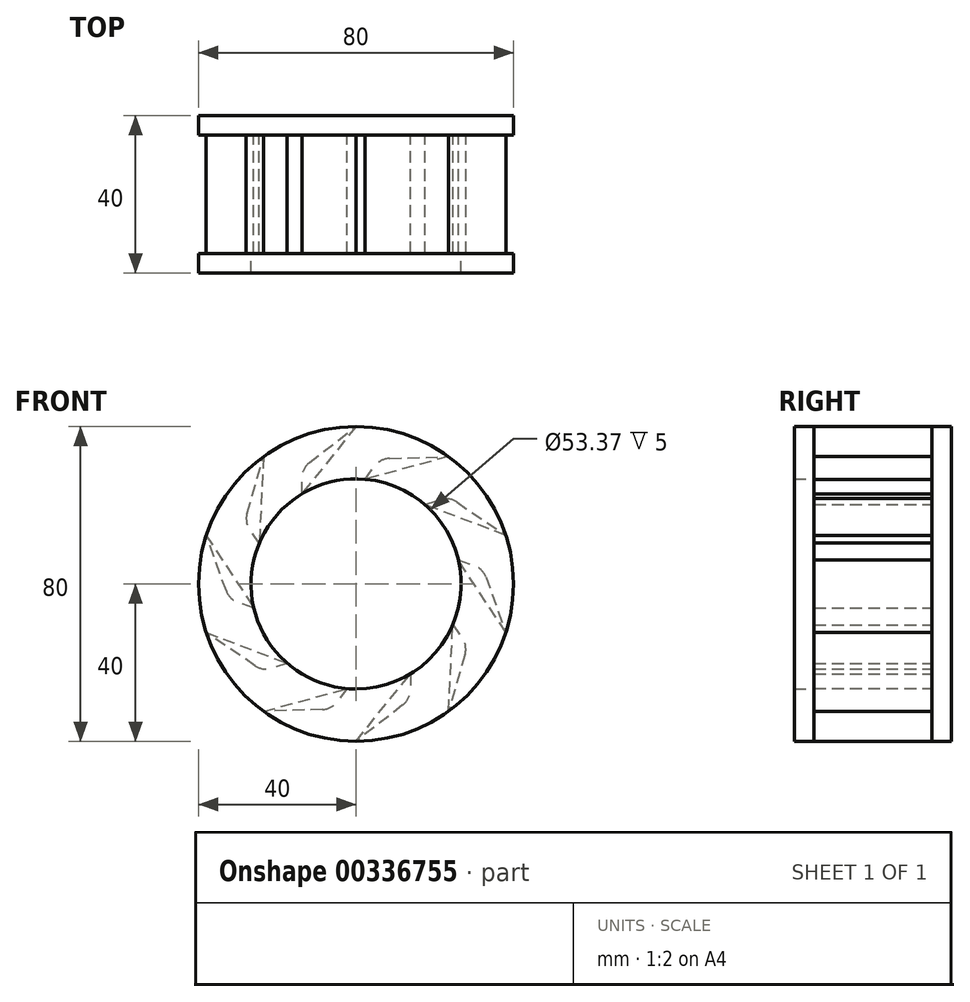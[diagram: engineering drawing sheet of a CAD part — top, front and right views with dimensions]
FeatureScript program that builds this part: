
annotation { "Feature Type Name" : "Feature", "Feature Type Description" : "" }
export const myFeature = defineFeature(function(context is Context, id is Id, definition is map)
    precondition{}
    {
        {
            var Q0;
            Q0=qCreatedBy(makeId("Front.planeOp"),FACE);
            var sketch = newSketch(context, id + "F0", { "sketchPlane" : qUnion([Q0])});
            skLineSegment(sketch, "E0", {"start": v(0, 55.71) * mm, "end": v(0, -58.93) * mm, "construction": true});
            skLineSegment(sketch, "E1", {"start": v(-76.6, 0) * mm, "end": v(92.9, 0) * mm, "construction": true});
            skCircle(sketch, "E2", {"center": v(0, 0) * mm, "radius": 40 * mm});
            skSolve(sketch);
        }
        {
            var Q0;
            Q0=makeQuery(id+"F0.imprint","IMPRINT",FACE,{"disambiguationData":[TD([[makeQuery(id+"F0.imprint","IMPRINT",EDGE,{"derivedFrom":sQuery(id+"F0.wireOp",EDGE,"E2")}),1.0]])]});
            extrude(context, id + "F1", {"entities" : qUnion([Q0]), "depth" : 5 * mm});
        }
        {
            var Q0;
            Q0=makeQuery(id+"F1.opExtrude","CAP_FACE",FACE,{"disambiguationData":[OSD([sQuery(id+"F0.wireOp",EDGE,"E2")])],"isStart":false});
            var sketch = newSketch(context, id + "F2", { "sketchPlane" : qUnion([Q0])});
            skLineSegment(sketch, "E3", {"start": v(0, 40) * mm, "end": v(-13.78, 22.85) * mm});
            skLineSegment(sketch, "E4", {"start": v(-13.78, 22.85) * mm, "end": v(-13.78, 26.85) * mm});
            skLineSegment(sketch, "E5", {"start": v(-11.85, 30.8) * mm, "end": v(0, 40) * mm});
            skPoint(sketch, "E6.visualSharp", {"position": v(-13.78, 29.3) * mm});
            skArc(sketch, "E6.filletArc", {"start": v(-11.85, 30.8) * mm, "mid": v(-13.27, 29.05) * mm, "end": v(-13.78, 26.85) * mm});
            skLineSegment(sketch, "E7.1.0", {"start": v(-27.69, 17.95) * mm, "end": v(-23.51, 32.36) * mm});
            skArc(sketch, "E7.1.1", {"start": v(-27.69, 17.95) * mm, "mid": v(-27.81, 15.7) * mm, "end": v(-26.93, 13.62) * mm});
            skLineSegment(sketch, "E7.1.2", {"start": v(-24.58, 10.39) * mm, "end": v(-26.93, 13.62) * mm});
            skLineSegment(sketch, "E7.1.3", {"start": v(-23.51, 32.36) * mm, "end": v(-24.58, 10.39) * mm});
            skLineSegment(sketch, "E7.2.0", {"start": v(-32.95, -1.75) * mm, "end": v(-38.04, 12.36) * mm});
            skArc(sketch, "E7.2.1", {"start": v(-32.95, -1.75) * mm, "mid": v(-31.73, -3.65) * mm, "end": v(-29.8, -4.8) * mm});
            skLineSegment(sketch, "E7.2.2", {"start": v(-26, -6.04) * mm, "end": v(-29.8, -4.8) * mm});
            skLineSegment(sketch, "E7.2.3", {"start": v(-38.04, 12.36) * mm, "end": v(-26, -6.04) * mm});
            skLineSegment(sketch, "E7.3.0", {"start": v(-25.63, -20.79) * mm, "end": v(-38.04, -12.36) * mm});
            skArc(sketch, "E7.3.1", {"start": v(-25.63, -20.79) * mm, "mid": v(-23.53, -21.6) * mm, "end": v(-21.28, -21.4) * mm});
            skLineSegment(sketch, "E7.3.2", {"start": v(-17.47, -20.17) * mm, "end": v(-21.28, -21.4) * mm});
            skLineSegment(sketch, "E7.3.3", {"start": v(-38.04, -12.36) * mm, "end": v(-17.47, -20.17) * mm});
            skLineSegment(sketch, "E7.4.0", {"start": v(-8.52, -31.88) * mm, "end": v(-23.51, -32.36) * mm});
            skArc(sketch, "E7.4.1", {"start": v(-8.52, -31.88) * mm, "mid": v(-6.34, -31.3) * mm, "end": v(-4.63, -29.82) * mm});
            skLineSegment(sketch, "E7.4.2", {"start": v(-2.28, -26.59) * mm, "end": v(-4.63, -29.82) * mm});
            skLineSegment(sketch, "E7.4.3", {"start": v(-23.51, -32.36) * mm, "end": v(-2.28, -26.59) * mm});
            skLineSegment(sketch, "E7.5.0", {"start": v(11.85, -30.8) * mm, "end": v(0, -40) * mm});
            skArc(sketch, "E7.5.1", {"start": v(11.85, -30.8) * mm, "mid": v(13.27, -29.05) * mm, "end": v(13.78, -26.85) * mm});
            skLineSegment(sketch, "E7.5.2", {"start": v(13.78, -22.85) * mm, "end": v(13.78, -26.85) * mm});
            skLineSegment(sketch, "E7.5.3", {"start": v(0, -40) * mm, "end": v(13.78, -22.85) * mm});
            skLineSegment(sketch, "E7.6.0", {"start": v(27.69, -17.95) * mm, "end": v(23.51, -32.36) * mm});
            skArc(sketch, "E7.6.1", {"start": v(27.69, -17.95) * mm, "mid": v(27.81, -15.7) * mm, "end": v(26.93, -13.62) * mm});
            skLineSegment(sketch, "E7.6.2", {"start": v(24.58, -10.39) * mm, "end": v(26.93, -13.62) * mm});
            skLineSegment(sketch, "E7.6.3", {"start": v(23.51, -32.36) * mm, "end": v(24.58, -10.39) * mm});
            skLineSegment(sketch, "E7.7.0", {"start": v(32.95, 1.75) * mm, "end": v(38.04, -12.36) * mm});
            skArc(sketch, "E7.7.1", {"start": v(32.95, 1.75) * mm, "mid": v(31.73, 3.65) * mm, "end": v(29.8, 4.8) * mm});
            skLineSegment(sketch, "E7.7.2", {"start": v(26, 6.04) * mm, "end": v(29.8, 4.8) * mm});
            skLineSegment(sketch, "E7.7.3", {"start": v(38.04, -12.36) * mm, "end": v(26, 6.04) * mm});
            skLineSegment(sketch, "E7.8.0", {"start": v(25.63, 20.79) * mm, "end": v(38.04, 12.36) * mm});
            skArc(sketch, "E7.8.1", {"start": v(25.63, 20.79) * mm, "mid": v(23.53, 21.6) * mm, "end": v(21.28, 21.4) * mm});
            skLineSegment(sketch, "E7.8.2", {"start": v(17.47, 20.17) * mm, "end": v(21.28, 21.4) * mm});
            skLineSegment(sketch, "E7.8.3", {"start": v(38.04, 12.36) * mm, "end": v(17.47, 20.17) * mm});
            skLineSegment(sketch, "E7.9.0", {"start": v(8.52, 31.88) * mm, "end": v(23.51, 32.36) * mm});
            skArc(sketch, "E7.9.1", {"start": v(8.52, 31.88) * mm, "mid": v(6.34, 31.3) * mm, "end": v(4.63, 29.82) * mm});
            skLineSegment(sketch, "E7.9.2", {"start": v(2.28, 26.59) * mm, "end": v(4.63, 29.82) * mm});
            skLineSegment(sketch, "E7.9.3", {"start": v(23.51, 32.36) * mm, "end": v(2.28, 26.59) * mm});
            skPoint(sketch, "E7.center", {"position": v(0, 0) * mm});
            skSolve(sketch);
        }
        {
            var Q0;
            Q0 = qSketchRegion(id + "F2", true);
            extrude(context, id + "F3", {"entities" : qUnion([Q0]), "operationType" : NewBodyOperationType.ADD, "depth" : 30 * mm});
        }
        {
            var Q0;
            Q0=qCreatedBy(makeId("Front.planeOp"),FACE);
            cPlane(context, id + "F4", {"entities" : qUnion([Q0]), "cplaneType" : CPlaneType.OFFSET, "offset" : 35 * mm, "width" : 150 * mm, "height" : 150 * mm});
        }
        {
            var Q0;
            Q0=qCreatedBy(id+"F4.planeOp",FACE);
            var sketch = newSketch(context, id + "F5", { "sketchPlane" : qUnion([Q0])});
            skCircle(sketch, "E8", {"center": v(0, 0) * mm, "radius": 40 * mm});
            skCircle(sketch, "E9", {"center": v(0, 0) * mm, "radius": 26.68 * mm});
            skSolve(sketch);
        }
        {
            var Q0;
            Q0 = qSketchRegion(id + "F5", true);
            extrude(context, id + "F6", {"entities" : qUnion([Q0]), "operationType" : NewBodyOperationType.ADD, "depth" : 5 * mm});
        }
        {
            var Q0;
            Q0=makeQuery(id+"F1.opExtrude","CAP_FACE",FACE,{"disambiguationData":[OSD([sQuery(id+"F0.wireOp",EDGE,"E2")])],"isStart":false});
            var sketch = newSketch(context, id + "F7", { "sketchPlane" : qUnion([Q0])});
            skCircle(sketch, "E10", {"center": v(0, 0) * mm, "radius": 1 * mm});
            skSolve(sketch);
        }
        {
            var Q0;
            Q0=sQuery(id+"F7.wireOp",EDGE,"E10");
            extrude(context, id + "F8", {"bodyType" : ToolBodyType.SURFACE, "operationType" : NewBodyOperationType.REMOVE, "surfaceEntities" : qUnion([Q0]), "oppositeDirection" : true, "depth" : 5 * mm});
        }
    });
